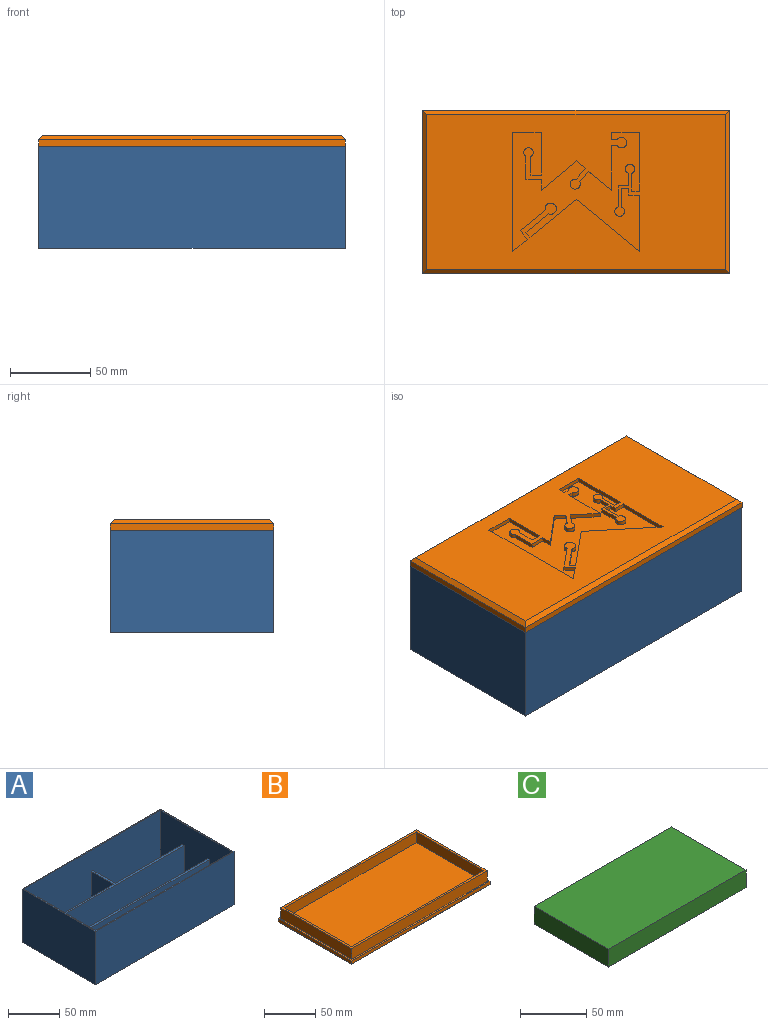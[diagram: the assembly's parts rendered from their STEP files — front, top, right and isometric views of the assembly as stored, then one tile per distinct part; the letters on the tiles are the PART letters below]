
ASSEMBLY  parts=3 mates=2
PART A: 23 faces, bbox 190.5x101.6x63.5 mm
  f0: plane 99.06x57.15mm, normal (-1,0,0), area 5500mm2, adj f1,f2,f3,f4,f10,f12,f14,f18
  f1: plane 187.96x31.75mm, normal (0,0,1), area 5967.7mm2, adj f0,f10,f11,f21
  f2: plane 187.96x57.15mm, normal (0,-1,0), area 10661.3mm2, adj f0,f3,f11,f12,f13,f15,f16,f19
  f3: plane 92.71x30.48mm, normal (0,0,1), area 2825.8mm2, adj f0,f2,f14,f15
  f4: plane 187.96x31.75mm, normal (0,0,1), area 5967.7mm2, adj f0,f11,f18,f20
  f5: plane 190.5x63.5mm, normal (0,1,0), area 12096.8mm2, adj f6,f8,f9,f12
  f6: plane 101.6x63.5mm, normal (-1,0,0), area 6451.6mm2, adj f5,f7,f9,f12
  f7: plane 190.5x63.5mm, normal (0,-1,0), area 12096.8mm2, adj f6,f8,f9,f12
  f8: plane 101.6x63.5mm, normal (1,0,0), area 6451.6mm2, adj f5,f7,f9,f12
  f9: plane 190.5x101.6mm, normal (0,0,-1), area 19354.8mm2, adj f5,f6,f7,f8
  f10: plane 187.96x57.15mm, normal (0,1,0), area 10741.9mm2, adj f0,f1,f11,f12
  f11: plane 99.06x57.15mm, normal (1,0,0), area 5500mm2, adj f1,f2,f4,f10,f12,f13,f17,f18
  f12: plane 190.5x101.6mm, normal (0,0,1), area 735.5mm2, adj f0,f2,f5,f6,f7,f8,f10,f11
  f13: plane 92.71x30.48mm, normal (0,0,1), area 2825.8mm2, adj f2,f11,f16,f17
  f14: plane 92.71x31.75mm, normal (0,1,0), area 2943.5mm2, adj f0,f3,f15,f19
  f15: plane 31.75x30.48mm, normal (1,0,0), area 967.7mm2, adj f2,f3,f14,f19
  f16: plane 31.75x30.48mm, normal (-1,0,0), area 967.7mm2, adj f2,f13,f17,f19
  f17: plane 92.71x31.75mm, normal (0,1,0), area 2943.5mm2, adj f11,f13,f16,f19
  f18: plane 187.96x31.75mm, normal (0,-1,0), area 5967.7mm2, adj f0,f4,f11,f19
  f19: plane 187.96x33.02mm, normal (0,0,1), area 554.8mm2, adj f0,f2,f11,f14,f15,f16,f17,f18
  f20: plane 187.96x31.75mm, normal (0,1,0), area 5967.7mm2, adj f0,f4,f11,f22
  f21: plane 187.96x31.75mm, normal (0,-1,0), area 5967.7mm2, adj f0,f1,f11,f22
  f22: plane 187.96x2.54mm, normal (0,0,1), area 477.4mm2, adj f0,f11,f20,f21
PART B: 63 faces, bbox 190.5x101.6x19.1 mm
  f0: plane 190.5x3.81mm, normal (0,1,0), area 725.8mm2, adj f1,f3,f4,f17
  f1: plane 101.6x3.81mm, normal (-1,0,0), area 387.1mm2, adj f0,f2,f4,f16
  f2: plane 190.5x3.81mm, normal (0,-1,0), area 725.8mm2, adj f1,f3,f4,f18
  f3: plane 101.6x3.81mm, normal (1,0,0), area 387.1mm2, adj f0,f2,f4,f19
  f4: plane 190.5x101.6mm, normal (0,0,1), area 1170.6mm2, adj f0,f1,f2,f3,f8,f9,f10,f11
  f5: plane 185.42x96.52mm, normal (0,0,-1), area 14927.6mm2, adj f16,f17,f18,f19,f20,f21,f22,f23
  f6: plane 181.36x92.46mm, normal (0,0,1), area 16767.5mm2, adj f12,f13,f14,f15
  f7: plane 186.44x97.54mm, normal (0,0,1), area 1416.8mm2, adj f8,f9,f10,f11,f12,f13,f14,f15
  f8: plane 186.44x12.7mm, normal (0,-1,0), area 2367.7mm2, adj f4,f7,f9,f11
  f9: plane 97.54x12.7mm, normal (-1,0,0), area 1238.7mm2, adj f4,f7,f8,f10
  f10: plane 186.44x12.7mm, normal (0,1,0), area 2367.7mm2, adj f4,f7,f9,f11
  f11: plane 97.54x12.7mm, normal (1,0,0), area 1238.7mm2, adj f4,f7,f8,f10
  f12: plane 181.36x12.7mm, normal (0,1,0), area 2303.2mm2, adj f6,f7,f13,f15
  f13: plane 92.46x12.7mm, normal (1,0,0), area 1174.2mm2, adj f6,f7,f12,f14
  f14: plane 181.36x12.7mm, normal (0,-1,0), area 2303.2mm2, adj f6,f7,f13,f15
  f15: plane 92.46x12.7mm, normal (-1,0,0), area 1174.2mm2, adj f6,f7,f12,f14
  f16: plane 101.6x2.54mm, normal (-0.71,0,-0.71), area 355.8mm2, adj f1,f5,f17,f18
  f17: plane 190.5x2.54mm, normal (0,0.71,-0.71), area 675.2mm2, adj f0,f5,f16,f19
  f18: plane 190.5x2.54mm, normal (0,-0.71,-0.71), area 675.2mm2, adj f2,f5,f16,f19
  f19: plane 101.6x2.54mm, normal (0.71,0,-0.71), area 355.8mm2, adj f3,f5,f17,f18
  f20: plane 6.74x5.55mm, normal (0.77,0.64,0), area 22.2mm2, adj f5,f21,f61,f62
  f21: plane 5.61x4.62mm, normal (0.64,-0.77,0), area 18.5mm2, adj f5,f20,f22,f62
  f22: plane 21.83x18.37mm, normal (-0.64,-0.77,0), area 72.5mm2, adj f5,f21,f23,f62
  f23: plane 6.67x2.54mm, normal (1,0,0), area 16.9mm2, adj f5,f22,f24,f62
  f24: plane 9.44x2.54mm, normal (0,-1,0), area 24mm2, adj f5,f23,f25,f62
  f25: plane 14.3x2.54mm, normal (1,0,0), area 36.3mm2, adj f5,f24,f26,f62
  f26: cylinder r=2.99mm len=5.98mm, axis (0,0,-1), area 39.4mm2, adj f5,f25,f27,f62
  f27: plane 11.4x2.54mm, normal (-1,0,0), area 29mm2, adj f5,f26,f28,f62
  f28: plane 6.32x2.54mm, normal (0,1,0), area 16.1mm2, adj f5,f27,f29,f62
  f29: plane 26.61x2.54mm, normal (1,0,0), area 67.6mm2, adj f5,f28,f30,f62
  f30: plane 17.81x2.54mm, normal (0,-1,0), area 45.2mm2, adj f5,f29,f31,f62
  f31: plane 74.22x2.54mm, normal (-1,0,0), area 188.5mm2, adj f5,f30,f32,f62
  f32: plane 9.27x7.62mm, normal (0.63,0.77,0), area 30.5mm2, adj f5,f31,f33,f62
  f33: plane 5.4x4.44mm, normal (0.77,-0.63,0), area 17.8mm2, adj f5,f32,f34,f62
  f34: plane 15.62x12.84mm, normal (0.63,0.77,0), area 51.4mm2, adj f5,f33,f35,f62
  f35: cylinder r=3.47mm len=6.94mm, axis (0,0,-1), area 47.3mm2, adj f5,f34,f36,f62
  f36: plane 14.02x11.52mm, normal (-0.63,-0.77,0), area 46.1mm2, adj f5,f35,f37,f62
  f37: plane 3.04x2.54mm, normal (-0.77,0.63,0), area 10mm2, adj f5,f36,f38,f62
  f38: plane 28.75x23.62mm, normal (0.63,0.77,0), area 94.5mm2, adj f5,f37,f39,f62
  f39: plane 39.36x32.56mm, normal (-0.64,0.77,0), area 129.7mm2, adj f5,f38,f40,f62
  f40: plane 35.06x2.54mm, normal (1,0,0), area 89.1mm2, adj f5,f39,f41,f62
  f41: plane 6.79x2.54mm, normal (0,-1,0), area 17.2mm2, adj f5,f40,f42,f62
  f42: plane 4.24x2.54mm, normal (1,0,0), area 10.8mm2, adj f5,f41,f43,f62
  f43: plane 4.52x2.54mm, normal (0,-1,0), area 11.5mm2, adj f5,f42,f44,f62
  f44: plane 11.45x2.54mm, normal (-1,0,0), area 29.1mm2, adj f5,f43,f45,f62
  f45: cylinder r=3.04mm len=6.08mm, axis (0,0,-1), area 43.4mm2, adj f5,f44,f46,f62
  f46: plane 13.01x2.54mm, normal (1,0,0), area 33mm2, adj f5,f45,f47,f62
  f47: plane 6.5x2.54mm, normal (0,1,0), area 16.5mm2, adj f5,f46,f48,f62
  f48: plane 7.78x2.54mm, normal (1,0,0), area 19.7mm2, adj f5,f47,f49,f62
  f49: cylinder r=2.89mm len=5.78mm, axis (0,0,-1), area 41.4mm2, adj f5,f48,f50,f62
  f50: plane 11.03x2.54mm, normal (-1,0,0), area 28mm2, adj f5,f49,f51,f62
  f51: plane 4.95x2.54mm, normal (0,1,0), area 12.6mm2, adj f5,f50,f52,f62
  f52: plane 36.61x2.54mm, normal (1,0,0), area 93mm2, adj f5,f51,f53,f62
  f53: plane 17.25x2.54mm, normal (0,-1,0), area 43.8mm2, adj f5,f52,f54,f62
  f54: plane 4.81x2.54mm, normal (-1,0,0), area 12.2mm2, adj f5,f53,f55,f62
  f55: plane 3.25x2.54mm, normal (0,1,0), area 8.3mm2, adj f5,f54,f56,f62
  f56: cylinder r=3.27mm len=6.54mm, axis (0,0,-1), area 43.1mm2, adj f5,f55,f57,f62
  f57: plane 3.25x2.54mm, normal (0,-1,0), area 8.3mm2, adj f5,f56,f58,f62
  f58: plane 27.99x2.54mm, normal (-1,0,0), area 71.1mm2, adj f5,f57,f59,f62
  f59: plane 14.42x11.88mm, normal (0.64,-0.77,0), area 47.4mm2, adj f5,f58,f60,f62
  f60: plane 6.64x5.46mm, normal (-0.77,-0.64,0), area 21.8mm2, adj f5,f59,f61,f62
  f61: cylinder r=3.14mm len=6.27mm, axis (0,0,-1), area 42.7mm2, adj f5,f20,f60,f62
  f62: plane 78.98x74.22mm, normal (0,0,-1), area 2969.1mm2, adj f20,f21,f22,f23,f24,f25,f26,f27
PART C: 6 faces, bbox 147.3x79.8x16.5 mm
  f0: plane 79.76x16.51mm, normal (1,0,0), area 1316.8mm2, adj f1,f3,f4,f5
  f1: plane 147.32x16.51mm, normal (0,1,0), area 2432.3mm2, adj f0,f2,f4,f5
  f2: plane 79.76x16.51mm, normal (-1,0,0), area 1316.8mm2, adj f1,f3,f4,f5
  f3: plane 147.32x16.51mm, normal (0,-1,0), area 2432.3mm2, adj f0,f2,f4,f5
  f4: plane 147.32x79.76mm, normal (0,0,1), area 11749.7mm2, adj f0,f1,f2,f3
  f5: plane 147.32x79.76mm, normal (0,0,-1), area 11749.7mm2, adj f0,f1,f2,f3
PLACE A rot(axis=(0,0,1),0deg) t=(-190.5,101.6,0)mm
PLACE B rot(axis=(0,1,0),180deg) t=(0,101.6,69.85)mm
PLACE C rot(axis=(0,1,0),180deg) t=(-147.27,-26.65,63.5)mm
MATE slider B.f4 <-> A.f12  axis (0,0,-1) through (-190.5,101.6,63.5)mm
MATE slider B.f6 <-> C.f5  axis (0,0,-1) through (-86.36,49.02,63.5)mm
